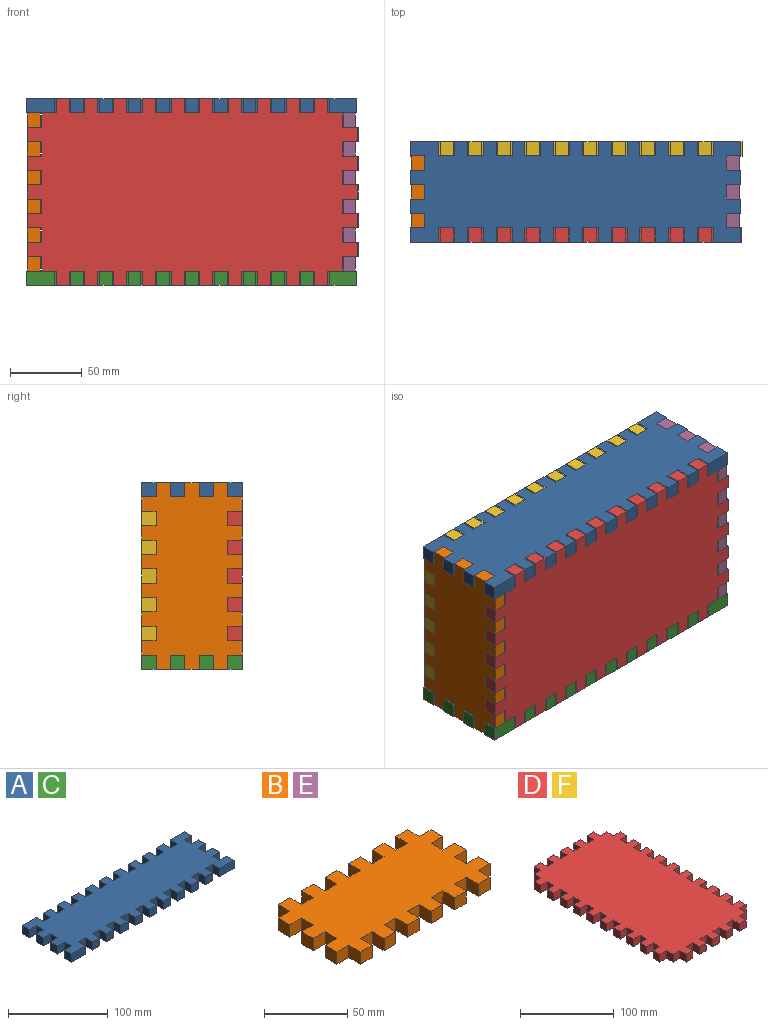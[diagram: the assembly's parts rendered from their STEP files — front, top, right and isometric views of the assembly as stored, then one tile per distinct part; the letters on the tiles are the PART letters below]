
ASSEMBLY  parts=6 mates=5
PART A: 110 faces, bbox 230x70x10 mm
  f0: plane 10x10mm, normal (-1,0,0), area 100mm2, adj f1,f107,f108,f109
  f1: plane 20x10mm, normal (0,-1,0), area 200mm2, adj f0,f2,f108,f109
  f2: plane 10x10mm, normal (1,0,0), area 100mm2, adj f1,f3,f108,f109
  f3: plane 10x10mm, normal (0,-1,0), area 100mm2, adj f2,f4,f108,f109
  f4: plane 10x10mm, normal (-1,0,0), area 100mm2, adj f3,f5,f108,f109
  f5: plane 10x10mm, normal (0,-1,0), area 100mm2, adj f4,f6,f108,f109
  f6: plane 10x10mm, normal (1,0,0), area 100mm2, adj f5,f7,f108,f109
  f7: plane 10x10mm, normal (0,-1,0), area 100mm2, adj f6,f8,f108,f109
  f8: plane 10x10mm, normal (-1,0,0), area 100mm2, adj f7,f9,f108,f109
  f9: plane 10x10mm, normal (0,-1,0), area 100mm2, adj f8,f10,f108,f109
  f10: plane 10x10mm, normal (1,0,0), area 100mm2, adj f9,f11,f108,f109
  f11: plane 10x10mm, normal (0,-1,0), area 100mm2, adj f10,f12,f108,f109
  f12: plane 10x10mm, normal (-1,0,0), area 100mm2, adj f11,f13,f108,f109
  f13: plane 10x10mm, normal (0,-1,0), area 100mm2, adj f12,f14,f108,f109
  f14: plane 10x10mm, normal (1,0,0), area 100mm2, adj f13,f15,f108,f109
  f15: plane 10x10mm, normal (0,-1,0), area 100mm2, adj f14,f16,f108,f109
  f16: plane 10x10mm, normal (-1,0,0), area 100mm2, adj f15,f17,f108,f109
  f17: plane 10x10mm, normal (0,-1,0), area 100mm2, adj f16,f18,f108,f109
  f18: plane 10x10mm, normal (1,0,0), area 100mm2, adj f17,f19,f108,f109
  f19: plane 10x10mm, normal (0,-1,0), area 100mm2, adj f18,f20,f108,f109
  f20: plane 10x10mm, normal (-1,0,0), area 100mm2, adj f19,f21,f108,f109
  f21: plane 10x10mm, normal (0,-1,0), area 100mm2, adj f20,f22,f108,f109
  f22: plane 10x10mm, normal (1,0,0), area 100mm2, adj f21,f23,f108,f109
  f23: plane 10x10mm, normal (0,-1,0), area 100mm2, adj f22,f24,f108,f109
  f24: plane 10x10mm, normal (-1,0,0), area 100mm2, adj f23,f25,f108,f109
  f25: plane 10x10mm, normal (0,-1,0), area 100mm2, adj f24,f26,f108,f109
  f26: plane 10x10mm, normal (1,0,0), area 100mm2, adj f25,f27,f108,f109
  f27: plane 10x10mm, normal (0,-1,0), area 100mm2, adj f26,f28,f108,f109
  f28: plane 10x10mm, normal (-1,0,0), area 100mm2, adj f27,f29,f108,f109
  f29: plane 10x10mm, normal (0,-1,0), area 100mm2, adj f28,f30,f108,f109
  f30: plane 10x10mm, normal (1,0,0), area 100mm2, adj f29,f31,f108,f109
  f31: plane 10x10mm, normal (0,-1,0), area 100mm2, adj f30,f32,f108,f109
  f32: plane 10x10mm, normal (-1,0,0), area 100mm2, adj f31,f33,f108,f109
  f33: plane 10x10mm, normal (0,-1,0), area 100mm2, adj f32,f34,f108,f109
  f34: plane 10x10mm, normal (1,0,0), area 100mm2, adj f33,f35,f108,f109
  f35: plane 10x10mm, normal (0,-1,0), area 100mm2, adj f34,f36,f108,f109
  f36: plane 10x10mm, normal (-1,0,0), area 100mm2, adj f35,f37,f108,f109
  f37: plane 10x10mm, normal (0,-1,0), area 100mm2, adj f36,f38,f108,f109
  f38: plane 10x10mm, normal (1,0,0), area 100mm2, adj f37,f39,f108,f109
  f39: plane 10x10mm, normal (0,-1,0), area 100mm2, adj f38,f40,f108,f109
  f40: plane 10x10mm, normal (-1,0,0), area 100mm2, adj f39,f41,f108,f109
  f41: plane 20x10mm, normal (0,-1,0), area 200mm2, adj f40,f42,f108,f109
  f42: plane 10x10mm, normal (1,0,0), area 100mm2, adj f41,f43,f108,f109
  f43: plane 10x10mm, normal (0,1,0), area 100mm2, adj f42,f44,f108,f109
  f44: plane 10x10mm, normal (1,0,0), area 100mm2, adj f43,f45,f108,f109
  f45: plane 10x10mm, normal (0,-1,0), area 100mm2, adj f44,f46,f108,f109
  f46: plane 10x10mm, normal (1,0,0), area 100mm2, adj f45,f47,f108,f109
  f47: plane 10x10mm, normal (0,1,0), area 100mm2, adj f46,f48,f108,f109
  f48: plane 10x10mm, normal (1,0,0), area 100mm2, adj f47,f49,f108,f109
  f49: plane 10x10mm, normal (0,-1,0), area 100mm2, adj f48,f50,f108,f109
  f50: plane 10x10mm, normal (1,0,0), area 100mm2, adj f49,f51,f108,f109
  f51: plane 10x10mm, normal (0,1,0), area 100mm2, adj f50,f52,f108,f109
  f52: plane 10x10mm, normal (1,0,0), area 100mm2, adj f51,f53,f108,f109
  f53: plane 10x10mm, normal (0,-1,0), area 100mm2, adj f52,f54,f108,f109
  f54: plane 10x10mm, normal (1,0,0), area 100mm2, adj f53,f55,f108,f109
  f55: plane 20x10mm, normal (0,1,0), area 200mm2, adj f54,f56,f108,f109
  f56: plane 10x10mm, normal (-1,0,0), area 100mm2, adj f55,f57,f108,f109
  f57: plane 10x10mm, normal (0,1,0), area 100mm2, adj f56,f58,f108,f109
  f58: plane 10x10mm, normal (1,0,0), area 100mm2, adj f57,f59,f108,f109
  f59: plane 10x10mm, normal (0,1,0), area 100mm2, adj f58,f60,f108,f109
  f60: plane 10x10mm, normal (-1,0,0), area 100mm2, adj f59,f61,f108,f109
  f61: plane 10x10mm, normal (0,1,0), area 100mm2, adj f60,f62,f108,f109
  f62: plane 10x10mm, normal (1,0,0), area 100mm2, adj f61,f63,f108,f109
  f63: plane 10x10mm, normal (0,1,0), area 100mm2, adj f62,f64,f108,f109
  f64: plane 10x10mm, normal (-1,0,0), area 100mm2, adj f63,f65,f108,f109
  f65: plane 10x10mm, normal (0,1,0), area 100mm2, adj f64,f66,f108,f109
  f66: plane 10x10mm, normal (1,0,0), area 100mm2, adj f65,f67,f108,f109
  f67: plane 10x10mm, normal (0,1,0), area 100mm2, adj f66,f68,f108,f109
  f68: plane 10x10mm, normal (-1,0,0), area 100mm2, adj f67,f69,f108,f109
  f69: plane 10x10mm, normal (0,1,0), area 100mm2, adj f68,f70,f108,f109
  f70: plane 10x10mm, normal (1,0,0), area 100mm2, adj f69,f71,f108,f109
  f71: plane 10x10mm, normal (0,1,0), area 100mm2, adj f70,f72,f108,f109
  f72: plane 10x10mm, normal (-1,0,0), area 100mm2, adj f71,f73,f108,f109
  f73: plane 10x10mm, normal (0,1,0), area 100mm2, adj f72,f74,f108,f109
  f74: plane 10x10mm, normal (1,0,0), area 100mm2, adj f73,f75,f108,f109
  f75: plane 10x10mm, normal (0,1,0), area 100mm2, adj f74,f76,f108,f109
  f76: plane 10x10mm, normal (-1,0,0), area 100mm2, adj f75,f77,f108,f109
  f77: plane 10x10mm, normal (0,1,0), area 100mm2, adj f76,f78,f108,f109
  f78: plane 10x10mm, normal (1,0,0), area 100mm2, adj f77,f79,f108,f109
  f79: plane 10x10mm, normal (0,1,0), area 100mm2, adj f78,f80,f108,f109
  f80: plane 10x10mm, normal (-1,0,0), area 100mm2, adj f79,f81,f108,f109
  f81: plane 10x10mm, normal (0,1,0), area 100mm2, adj f80,f82,f108,f109
  f82: plane 10x10mm, normal (1,0,0), area 100mm2, adj f81,f83,f108,f109
  f83: plane 10x10mm, normal (0,1,0), area 100mm2, adj f82,f84,f108,f109
  f84: plane 10x10mm, normal (-1,0,0), area 100mm2, adj f83,f85,f108,f109
  f85: plane 10x10mm, normal (0,1,0), area 100mm2, adj f84,f86,f108,f109
  f86: plane 10x10mm, normal (1,0,0), area 100mm2, adj f85,f87,f108,f109
  f87: plane 10x10mm, normal (0,1,0), area 100mm2, adj f86,f88,f108,f109
  f88: plane 10x10mm, normal (-1,0,0), area 100mm2, adj f87,f89,f108,f109
  f89: plane 10x10mm, normal (0,1,0), area 100mm2, adj f88,f90,f108,f109
  f90: plane 10x10mm, normal (1,0,0), area 100mm2, adj f89,f91,f108,f109
  f91: plane 10x10mm, normal (0,1,0), area 100mm2, adj f90,f92,f108,f109
  f92: plane 10x10mm, normal (-1,0,0), area 100mm2, adj f91,f93,f108,f109
  f93: plane 10x10mm, normal (0,1,0), area 100mm2, adj f92,f94,f108,f109
  f94: plane 10x10mm, normal (1,0,0), area 100mm2, adj f93,f95,f108,f109
  f95: plane 20x10mm, normal (0,1,0), area 200mm2, adj f94,f96,f108,f109
  f96: plane 10x10mm, normal (-1,0,0), area 100mm2, adj f95,f97,f108,f109
  f97: plane 10x10mm, normal (0,-1,0), area 100mm2, adj f96,f98,f108,f109
  f98: plane 10x10mm, normal (-1,0,0), area 100mm2, adj f97,f99,f108,f109
  f99: plane 10x10mm, normal (0,1,0), area 100mm2, adj f98,f100,f108,f109
  f100: plane 10x10mm, normal (-1,0,0), area 100mm2, adj f99,f101,f108,f109
  f101: plane 10x10mm, normal (0,-1,0), area 100mm2, adj f100,f102,f108,f109
  f102: plane 10x10mm, normal (-1,0,0), area 100mm2, adj f101,f103,f108,f109
  f103: plane 10x10mm, normal (0,1,0), area 100mm2, adj f102,f104,f108,f109
  f104: plane 10x10mm, normal (-1,0,0), area 100mm2, adj f103,f105,f108,f109
  f105: plane 10x10mm, normal (0,-1,0), area 100mm2, adj f104,f106,f108,f109
  f106: plane 10x10mm, normal (-1,0,0), area 100mm2, adj f105,f107,f108,f109
  f107: plane 10x10mm, normal (0,1,0), area 100mm2, adj f0,f106,f108,f109
  f108: plane 230x70mm, normal (0,0,1), area 13500mm2, adj f0,f1,f2,f3,f4,f5,f6,f7
  f109: plane 230x70mm, normal (0,0,-1), area 13500mm2, adj f0,f1,f2,f3,f4,f5,f6,f7
PART B: 70 faces, bbox 130x70x9 mm
  f0: plane 10x9mm, normal (-1,0,0), area 90mm2, adj f1,f67,f68,f69
  f1: plane 10x9mm, normal (0,-1,0), area 90mm2, adj f0,f2,f68,f69
  f2: plane 10x9mm, normal (1,0,0), area 90mm2, adj f1,f3,f68,f69
  f3: plane 10x9mm, normal (0,-1,0), area 90mm2, adj f2,f4,f68,f69
  f4: plane 10x9mm, normal (-1,0,0), area 90mm2, adj f3,f5,f68,f69
  f5: plane 10x9mm, normal (0,-1,0), area 90mm2, adj f4,f6,f68,f69
  f6: plane 10x9mm, normal (1,0,0), area 90mm2, adj f5,f7,f68,f69
  f7: plane 10x9mm, normal (0,-1,0), area 90mm2, adj f6,f8,f68,f69
  f8: plane 10x9mm, normal (-1,0,0), area 90mm2, adj f7,f9,f68,f69
  f9: plane 10x9mm, normal (0,-1,0), area 90mm2, adj f8,f10,f68,f69
  f10: plane 10x9mm, normal (1,0,0), area 90mm2, adj f9,f11,f68,f69
  f11: plane 10x9mm, normal (0,-1,0), area 90mm2, adj f10,f12,f68,f69
  f12: plane 10x9mm, normal (-1,0,0), area 90mm2, adj f11,f13,f68,f69
  f13: plane 10x9mm, normal (0,-1,0), area 90mm2, adj f12,f14,f68,f69
  f14: plane 10x9mm, normal (1,0,0), area 90mm2, adj f13,f15,f68,f69
  f15: plane 10x9mm, normal (0,-1,0), area 90mm2, adj f14,f16,f68,f69
  f16: plane 10x9mm, normal (-1,0,0), area 90mm2, adj f15,f17,f68,f69
  f17: plane 10x9mm, normal (0,-1,0), area 90mm2, adj f16,f18,f68,f69
  f18: plane 10x9mm, normal (1,0,0), area 90mm2, adj f17,f19,f68,f69
  f19: plane 10x9mm, normal (0,-1,0), area 90mm2, adj f18,f20,f68,f69
  f20: plane 10x9mm, normal (-1,0,0), area 90mm2, adj f19,f21,f68,f69
  f21: plane 10x9mm, normal (0,-1,0), area 90mm2, adj f20,f22,f68,f69
  f22: plane 10x9mm, normal (1,0,0), area 90mm2, adj f21,f23,f68,f69
  f23: plane 10x9mm, normal (0,-1,0), area 90mm2, adj f22,f24,f68,f69
  f24: plane 10x9mm, normal (1,0,0), area 90mm2, adj f23,f25,f68,f69
  f25: plane 10x9mm, normal (0,1,0), area 90mm2, adj f24,f26,f68,f69
  f26: plane 10x9mm, normal (1,0,0), area 90mm2, adj f25,f27,f68,f69
  f27: plane 10x9mm, normal (0,-1,0), area 90mm2, adj f26,f28,f68,f69
  f28: plane 10x9mm, normal (1,0,0), area 90mm2, adj f27,f29,f68,f69
  f29: plane 10x9mm, normal (0,1,0), area 90mm2, adj f28,f30,f68,f69
  f30: plane 10x9mm, normal (1,0,0), area 90mm2, adj f29,f31,f68,f69
  f31: plane 10x9mm, normal (0,-1,0), area 90mm2, adj f30,f32,f68,f69
  f32: plane 10x9mm, normal (1,0,0), area 90mm2, adj f31,f33,f68,f69
  f33: plane 10x9mm, normal (0,1,0), area 90mm2, adj f32,f34,f68,f69
  f34: plane 10x9mm, normal (1,0,0), area 90mm2, adj f33,f35,f68,f69
  f35: plane 10x9mm, normal (0,1,0), area 90mm2, adj f34,f36,f68,f69
  f36: plane 10x9mm, normal (-1,0,0), area 90mm2, adj f35,f37,f68,f69
  f37: plane 10x9mm, normal (0,1,0), area 90mm2, adj f36,f38,f68,f69
  f38: plane 10x9mm, normal (1,0,0), area 90mm2, adj f37,f39,f68,f69
  f39: plane 10x9mm, normal (0,1,0), area 90mm2, adj f38,f40,f68,f69
  f40: plane 10x9mm, normal (-1,0,0), area 90mm2, adj f39,f41,f68,f69
  f41: plane 10x9mm, normal (0,1,0), area 90mm2, adj f40,f42,f68,f69
  f42: plane 10x9mm, normal (1,0,0), area 90mm2, adj f41,f43,f68,f69
  f43: plane 10x9mm, normal (0,1,0), area 90mm2, adj f42,f44,f68,f69
  f44: plane 10x9mm, normal (-1,0,0), area 90mm2, adj f43,f45,f68,f69
  f45: plane 10x9mm, normal (0,1,0), area 90mm2, adj f44,f46,f68,f69
  f46: plane 10x9mm, normal (1,0,0), area 90mm2, adj f45,f47,f68,f69
  f47: plane 10x9mm, normal (0,1,0), area 90mm2, adj f46,f48,f68,f69
  f48: plane 10x9mm, normal (-1,0,0), area 90mm2, adj f47,f49,f68,f69
  f49: plane 10x9mm, normal (0,1,0), area 90mm2, adj f48,f50,f68,f69
  f50: plane 10x9mm, normal (1,0,0), area 90mm2, adj f49,f51,f68,f69
  f51: plane 10x9mm, normal (0,1,0), area 90mm2, adj f50,f52,f68,f69
  f52: plane 10x9mm, normal (-1,0,0), area 90mm2, adj f51,f53,f68,f69
  f53: plane 10x9mm, normal (0,1,0), area 90mm2, adj f52,f54,f68,f69
  f54: plane 10x9mm, normal (1,0,0), area 90mm2, adj f53,f55,f68,f69
  f55: plane 10x9mm, normal (0,1,0), area 90mm2, adj f54,f56,f68,f69
  f56: plane 10x9mm, normal (-1,0,0), area 90mm2, adj f55,f57,f68,f69
  f57: plane 10x9mm, normal (0,1,0), area 90mm2, adj f56,f58,f68,f69
  f58: plane 10x9mm, normal (-1,0,0), area 90mm2, adj f57,f59,f68,f69
  f59: plane 10x9mm, normal (0,-1,0), area 90mm2, adj f58,f60,f68,f69
  f60: plane 10x9mm, normal (-1,0,0), area 90mm2, adj f59,f61,f68,f69
  f61: plane 10x9mm, normal (0,1,0), area 90mm2, adj f60,f62,f68,f69
  f62: plane 10x9mm, normal (-1,0,0), area 90mm2, adj f61,f63,f68,f69
  f63: plane 10x9mm, normal (0,-1,0), area 90mm2, adj f62,f64,f68,f69
  f64: plane 10x9mm, normal (-1,0,0), area 90mm2, adj f63,f65,f68,f69
  f65: plane 10x9mm, normal (0,1,0), area 90mm2, adj f64,f66,f68,f69
  f66: plane 10x9mm, normal (-1,0,0), area 90mm2, adj f65,f67,f68,f69
  f67: plane 10x9mm, normal (0,-1,0), area 90mm2, adj f0,f66,f68,f69
  f68: plane 130x70mm, normal (0,0,1), area 7300mm2, adj f0,f1,f2,f3,f4,f5,f6,f7
  f69: plane 130x70mm, normal (0,0,-1), area 7300mm2, adj f0,f1,f2,f3,f4,f5,f6,f7
PART C: same geometry as A
PART D: 126 faces, bbox 130x230x10 mm
  f0: plane 10x10mm, normal (-1,0,0), area 100mm2, adj f1,f123,f124,f125
  f1: plane 10x10mm, normal (0,-1,0), area 100mm2, adj f0,f2,f124,f125
  f2: plane 10x10mm, normal (-1,0,0), area 100mm2, adj f1,f3,f124,f125
  f3: plane 10x10mm, normal (0,-1,0), area 100mm2, adj f2,f4,f124,f125
  f4: plane 10x10mm, normal (1,0,0), area 100mm2, adj f3,f5,f124,f125
  f5: plane 10x10mm, normal (0,-1,0), area 100mm2, adj f4,f6,f124,f125
  f6: plane 10x10mm, normal (-1,0,0), area 100mm2, adj f5,f7,f124,f125
  f7: plane 10x10mm, normal (0,-1,0), area 100mm2, adj f6,f8,f124,f125
  f8: plane 10x10mm, normal (1,0,0), area 100mm2, adj f7,f9,f124,f125
  f9: plane 10x10mm, normal (0,-1,0), area 100mm2, adj f8,f10,f124,f125
  f10: plane 10x10mm, normal (-1,0,0), area 100mm2, adj f9,f11,f124,f125
  f11: plane 10x10mm, normal (0,-1,0), area 100mm2, adj f10,f12,f124,f125
  f12: plane 10x10mm, normal (1,0,0), area 100mm2, adj f11,f13,f124,f125
  f13: plane 10x10mm, normal (0,-1,0), area 100mm2, adj f12,f14,f124,f125
  f14: plane 10x10mm, normal (-1,0,0), area 100mm2, adj f13,f15,f124,f125
  f15: plane 10x10mm, normal (0,-1,0), area 100mm2, adj f14,f16,f124,f125
  f16: plane 10x10mm, normal (1,0,0), area 100mm2, adj f15,f17,f124,f125
  f17: plane 10x10mm, normal (0,-1,0), area 100mm2, adj f16,f18,f124,f125
  f18: plane 10x10mm, normal (-1,0,0), area 100mm2, adj f17,f19,f124,f125
  f19: plane 10x10mm, normal (0,-1,0), area 100mm2, adj f18,f20,f124,f125
  f20: plane 10x10mm, normal (1,0,0), area 100mm2, adj f19,f21,f124,f125
  f21: plane 10x10mm, normal (0,-1,0), area 100mm2, adj f20,f22,f124,f125
  f22: plane 10x10mm, normal (1,0,0), area 100mm2, adj f21,f23,f124,f125
  f23: plane 10x10mm, normal (0,-1,0), area 100mm2, adj f22,f24,f124,f125
  f24: plane 10x10mm, normal (1,0,0), area 100mm2, adj f23,f25,f124,f125
  f25: plane 10x10mm, normal (0,1,0), area 100mm2, adj f24,f26,f124,f125
  f26: plane 10x10mm, normal (1,0,0), area 100mm2, adj f25,f27,f124,f125
  f27: plane 10x10mm, normal (0,-1,0), area 100mm2, adj f26,f28,f124,f125
  f28: plane 10x10mm, normal (1,0,0), area 100mm2, adj f27,f29,f124,f125
  f29: plane 10x10mm, normal (0,1,0), area 100mm2, adj f28,f30,f124,f125
  f30: plane 10x10mm, normal (1,0,0), area 100mm2, adj f29,f31,f124,f125
  f31: plane 10x10mm, normal (0,-1,0), area 100mm2, adj f30,f32,f124,f125
  f32: plane 10x10mm, normal (1,0,0), area 100mm2, adj f31,f33,f124,f125
  f33: plane 10x10mm, normal (0,1,0), area 100mm2, adj f32,f34,f124,f125
  f34: plane 10x10mm, normal (1,0,0), area 100mm2, adj f33,f35,f124,f125
  f35: plane 10x10mm, normal (0,-1,0), area 100mm2, adj f34,f36,f124,f125
  f36: plane 10x10mm, normal (1,0,0), area 100mm2, adj f35,f37,f124,f125
  f37: plane 10x10mm, normal (0,1,0), area 100mm2, adj f36,f38,f124,f125
  f38: plane 10x10mm, normal (1,0,0), area 100mm2, adj f37,f39,f124,f125
  f39: plane 10x10mm, normal (0,-1,0), area 100mm2, adj f38,f40,f124,f125
  f40: plane 10x10mm, normal (1,0,0), area 100mm2, adj f39,f41,f124,f125
  f41: plane 10x10mm, normal (0,1,0), area 100mm2, adj f40,f42,f124,f125
  f42: plane 10x10mm, normal (1,0,0), area 100mm2, adj f41,f43,f124,f125
  f43: plane 10x10mm, normal (0,-1,0), area 100mm2, adj f42,f44,f124,f125
  f44: plane 10x10mm, normal (1,0,0), area 100mm2, adj f43,f45,f124,f125
  f45: plane 10x10mm, normal (0,1,0), area 100mm2, adj f44,f46,f124,f125
  f46: plane 10x10mm, normal (1,0,0), area 100mm2, adj f45,f47,f124,f125
  f47: plane 10x10mm, normal (0,-1,0), area 100mm2, adj f46,f48,f124,f125
  f48: plane 10x10mm, normal (1,0,0), area 100mm2, adj f47,f49,f124,f125
  f49: plane 10x10mm, normal (0,1,0), area 100mm2, adj f48,f50,f124,f125
  f50: plane 10x10mm, normal (1,0,0), area 100mm2, adj f49,f51,f124,f125
  f51: plane 10x10mm, normal (0,-1,0), area 100mm2, adj f50,f52,f124,f125
  f52: plane 10x10mm, normal (1,0,0), area 100mm2, adj f51,f53,f124,f125
  f53: plane 10x10mm, normal (0,1,0), area 100mm2, adj f52,f54,f124,f125
  f54: plane 10x10mm, normal (1,0,0), area 100mm2, adj f53,f55,f124,f125
  f55: plane 10x10mm, normal (0,-1,0), area 100mm2, adj f54,f56,f124,f125
  f56: plane 10x10mm, normal (1,0,0), area 100mm2, adj f55,f57,f124,f125
  f57: plane 10x10mm, normal (0,1,0), area 100mm2, adj f56,f58,f124,f125
  f58: plane 10x10mm, normal (1,0,0), area 100mm2, adj f57,f59,f124,f125
  f59: plane 10x10mm, normal (0,-1,0), area 100mm2, adj f58,f60,f124,f125
  f60: plane 10x10mm, normal (1,0,0), area 100mm2, adj f59,f61,f124,f125
  f61: plane 10x10mm, normal (0,1,0), area 100mm2, adj f60,f62,f124,f125
  f62: plane 10x10mm, normal (1,0,0), area 100mm2, adj f61,f63,f124,f125
  f63: plane 10x10mm, normal (0,1,0), area 100mm2, adj f62,f64,f124,f125
  f64: plane 10x10mm, normal (1,0,0), area 100mm2, adj f63,f65,f124,f125
  f65: plane 10x10mm, normal (0,1,0), area 100mm2, adj f64,f66,f124,f125
  f66: plane 10x10mm, normal (-1,0,0), area 100mm2, adj f65,f67,f124,f125
  f67: plane 10x10mm, normal (0,1,0), area 100mm2, adj f66,f68,f124,f125
  f68: plane 10x10mm, normal (1,0,0), area 100mm2, adj f67,f69,f124,f125
  f69: plane 10x10mm, normal (0,1,0), area 100mm2, adj f68,f70,f124,f125
  f70: plane 10x10mm, normal (-1,0,0), area 100mm2, adj f69,f71,f124,f125
  f71: plane 10x10mm, normal (0,1,0), area 100mm2, adj f70,f72,f124,f125
  f72: plane 10x10mm, normal (1,0,0), area 100mm2, adj f71,f73,f124,f125
  f73: plane 10x10mm, normal (0,1,0), area 100mm2, adj f72,f74,f124,f125
  f74: plane 10x10mm, normal (-1,0,0), area 100mm2, adj f73,f75,f124,f125
  f75: plane 10x10mm, normal (0,1,0), area 100mm2, adj f74,f76,f124,f125
  f76: plane 10x10mm, normal (1,0,0), area 100mm2, adj f75,f77,f124,f125
  f77: plane 10x10mm, normal (0,1,0), area 100mm2, adj f76,f78,f124,f125
  f78: plane 10x10mm, normal (-1,0,0), area 100mm2, adj f77,f79,f124,f125
  f79: plane 10x10mm, normal (0,1,0), area 100mm2, adj f78,f80,f124,f125
  f80: plane 10x10mm, normal (1,0,0), area 100mm2, adj f79,f81,f124,f125
  f81: plane 10x10mm, normal (0,1,0), area 100mm2, adj f80,f82,f124,f125
  f82: plane 10x10mm, normal (-1,0,0), area 100mm2, adj f81,f83,f124,f125
  f83: plane 10x10mm, normal (0,1,0), area 100mm2, adj f82,f84,f124,f125
  f84: plane 10x10mm, normal (-1,0,0), area 100mm2, adj f83,f85,f124,f125
  f85: plane 10x10mm, normal (0,1,0), area 100mm2, adj f84,f86,f124,f125
  f86: plane 10x10mm, normal (-1,0,0), area 100mm2, adj f85,f87,f124,f125
  f87: plane 10x10mm, normal (0,-1,0), area 100mm2, adj f86,f88,f124,f125
  f88: plane 10x10mm, normal (-1,0,0), area 100mm2, adj f87,f89,f124,f125
  f89: plane 10x10mm, normal (0,1,0), area 100mm2, adj f88,f90,f124,f125
  f90: plane 10x10mm, normal (-1,0,0), area 100mm2, adj f89,f91,f124,f125
  f91: plane 10x10mm, normal (0,-1,0), area 100mm2, adj f90,f92,f124,f125
  f92: plane 10x10mm, normal (-1,0,0), area 100mm2, adj f91,f93,f124,f125
  f93: plane 10x10mm, normal (0,1,0), area 100mm2, adj f92,f94,f124,f125
  f94: plane 10x10mm, normal (-1,0,0), area 100mm2, adj f93,f95,f124,f125
  f95: plane 10x10mm, normal (0,-1,0), area 100mm2, adj f94,f96,f124,f125
  f96: plane 10x10mm, normal (-1,0,0), area 100mm2, adj f95,f97,f124,f125
  f97: plane 10x10mm, normal (0,1,0), area 100mm2, adj f96,f98,f124,f125
  f98: plane 10x10mm, normal (-1,0,0), area 100mm2, adj f97,f99,f124,f125
  f99: plane 10x10mm, normal (0,-1,0), area 100mm2, adj f98,f100,f124,f125
  f100: plane 10x10mm, normal (-1,0,0), area 100mm2, adj f99,f101,f124,f125
  f101: plane 10x10mm, normal (0,1,0), area 100mm2, adj f100,f102,f124,f125
  f102: plane 10x10mm, normal (-1,0,0), area 100mm2, adj f101,f103,f124,f125
  f103: plane 10x10mm, normal (0,-1,0), area 100mm2, adj f102,f104,f124,f125
  f104: plane 10x10mm, normal (-1,0,0), area 100mm2, adj f103,f105,f124,f125
  f105: plane 10x10mm, normal (0,1,0), area 100mm2, adj f104,f106,f124,f125
  f106: plane 10x10mm, normal (-1,0,0), area 100mm2, adj f105,f107,f124,f125
  f107: plane 10x10mm, normal (0,-1,0), area 100mm2, adj f106,f108,f124,f125
  f108: plane 10x10mm, normal (-1,0,0), area 100mm2, adj f107,f109,f124,f125
  f109: plane 10x10mm, normal (0,1,0), area 100mm2, adj f108,f110,f124,f125
  f110: plane 10x10mm, normal (-1,0,0), area 100mm2, adj f109,f111,f124,f125
  f111: plane 10x10mm, normal (0,-1,0), area 100mm2, adj f110,f112,f124,f125
  f112: plane 10x10mm, normal (-1,0,0), area 100mm2, adj f111,f113,f124,f125
  f113: plane 10x10mm, normal (0,1,0), area 100mm2, adj f112,f114,f124,f125
  f114: plane 10x10mm, normal (-1,0,0), area 100mm2, adj f113,f115,f124,f125
  f115: plane 10x10mm, normal (0,-1,0), area 100mm2, adj f114,f116,f124,f125
  f116: plane 10x10mm, normal (-1,0,0), area 100mm2, adj f115,f117,f124,f125
  f117: plane 10x10mm, normal (0,1,0), area 100mm2, adj f116,f118,f124,f125
  f118: plane 10x10mm, normal (-1,0,0), area 100mm2, adj f117,f119,f124,f125
  f119: plane 10x10mm, normal (0,-1,0), area 100mm2, adj f118,f120,f124,f125
  f120: plane 10x10mm, normal (-1,0,0), area 100mm2, adj f119,f121,f124,f125
  f121: plane 10x10mm, normal (0,1,0), area 100mm2, adj f120,f122,f124,f125
  f122: plane 10x10mm, normal (-1,0,0), area 100mm2, adj f121,f123,f124,f125
  f123: plane 10x10mm, normal (0,-1,0), area 100mm2, adj f0,f122,f124,f125
  f124: plane 230x130mm, normal (0,0,1), area 26100mm2, adj f0,f1,f2,f3,f4,f5,f6,f7
  f125: plane 230x130mm, normal (0,0,-1), area 26100mm2, adj f0,f1,f2,f3,f4,f5,f6,f7
PART E: same geometry as B
PART F: same geometry as D
PLACE A t=(-97.83,45.17,-10.53)mm
PLACE B rot(axis=(0,-1,0),90deg) t=(-87.83,45.17,-120.53)mm
PLACE C t=(-97.83,45.17,-130.53)mm
PLACE D rot(axis=(-0.58,0.58,0.58),120deg) t=(123.17,45.17,-10.53)mm
PLACE E rot(axis=(0,1,0),90deg) t=(122.17,45.17,-10.53)mm
PLACE F rot(axis=(-0.58,-0.58,-0.58),120deg) t=(-86.83,105.17,-120.53)mm
MATE slider D.f124 <-> B.f3  axis (0,1,0) through (-96.83,55.17,-110.53)mm
MATE slider F.f125 <-> B.f37  axis (0,-1,0) through (-96.83,105.17,-20.53)mm
MATE slider B.f69 <-> C.f98  axis (1,0,0) through (-87.83,105.17,-130.53)mm
MATE slider E.f69 <-> A.f52  axis (-1,0,0) through (122.17,105.17,-0.53)mm
MATE slider C.f52 <-> E.f69  axis (1,0,0) through (122.17,105.17,-130.53)mm
